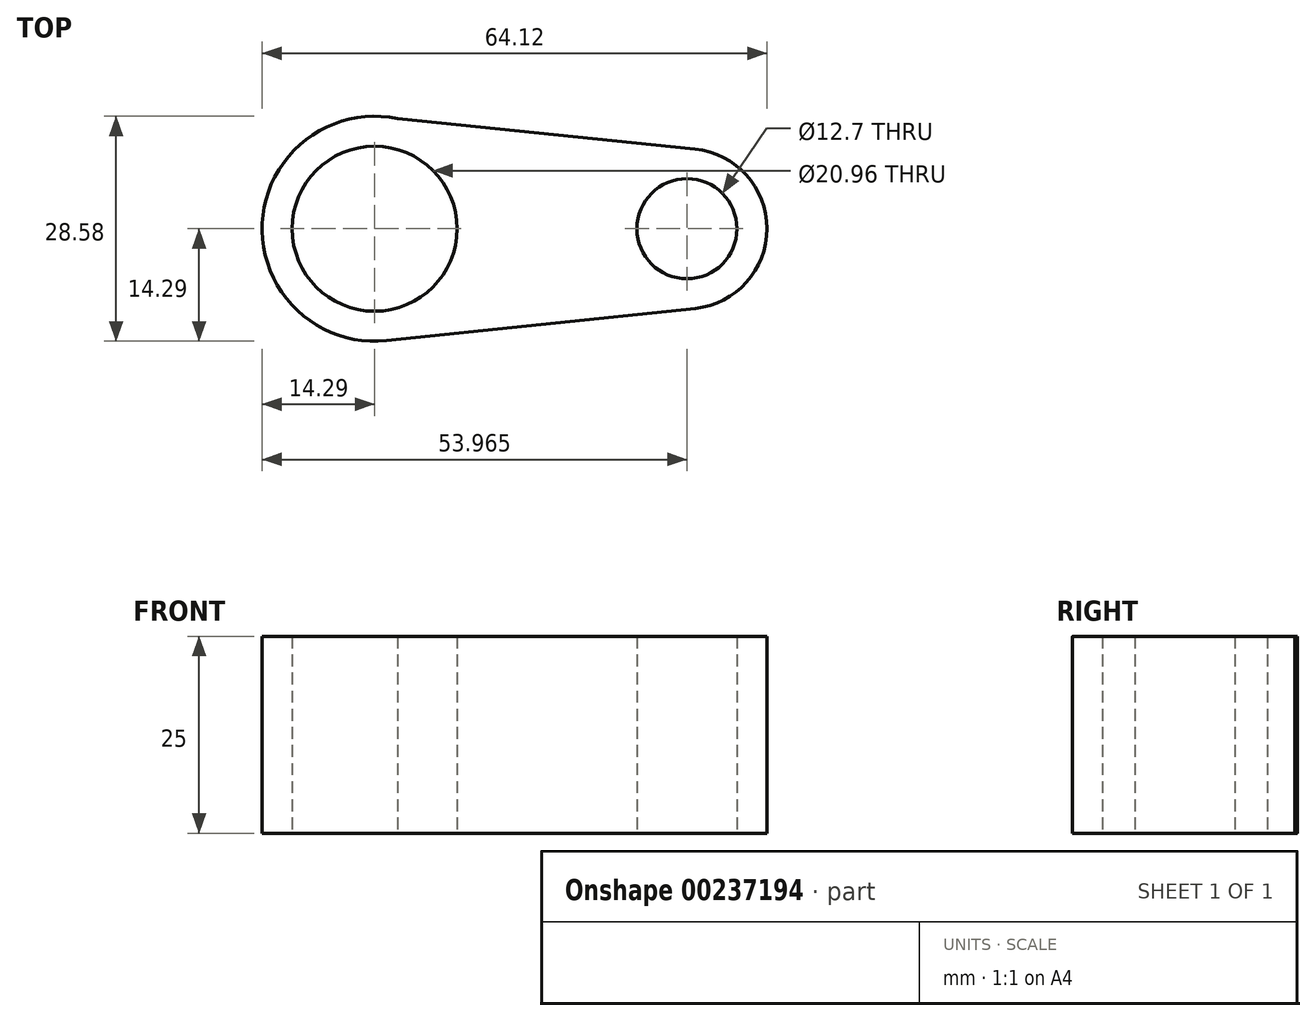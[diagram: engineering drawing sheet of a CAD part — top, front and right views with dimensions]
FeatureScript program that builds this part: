
annotation { "Feature Type Name" : "Feature", "Feature Type Description" : "" }
export const myFeature = defineFeature(function(context is Context, id is Id, definition is map)
    precondition{}
    {
        {
            var Q0;
            Q0=qCreatedBy(makeId("Top.planeOp"),FACE);
            var sketch = newSketch(context, id + "F0", { "sketchPlane" : qUnion([Q0])});
            skCircle(sketch, "E0", {"center": v(0, 0) * mm, "radius": 10.48 * mm});
            skLineSegment(sketch, "E1", {"start": v(0, 0) * mm, "end": v(39.67, 0) * mm, "construction": true});
            skCircle(sketch, "E2", {"center": v(39.67, 0) * mm, "radius": 6.35 * mm});
            skCircle(sketch, "E3", {"center": v(0, 0) * mm, "radius": 14.29 * mm});
            skCircle(sketch, "E4", {"center": v(39.67, 0) * mm, "radius": 10.16 * mm});
            skLineSegment(sketch, "E5", {"start": v(0, 14.29) * mm, "end": v(40.71, 10.1) * mm});
            skLineSegment(sketch, "E6", {"start": v(40.73, -10.1) * mm, "end": v(1.49, -14.2) * mm});
            skSolve(sketch);
        }
        {
            var Q0;
            Q0 = qSketchRegion(id + "F0", true);
            extrude(context, id + "F1", {"entities" : qUnion([Q0]), "depth" : 25 * mm});
        }
    });
